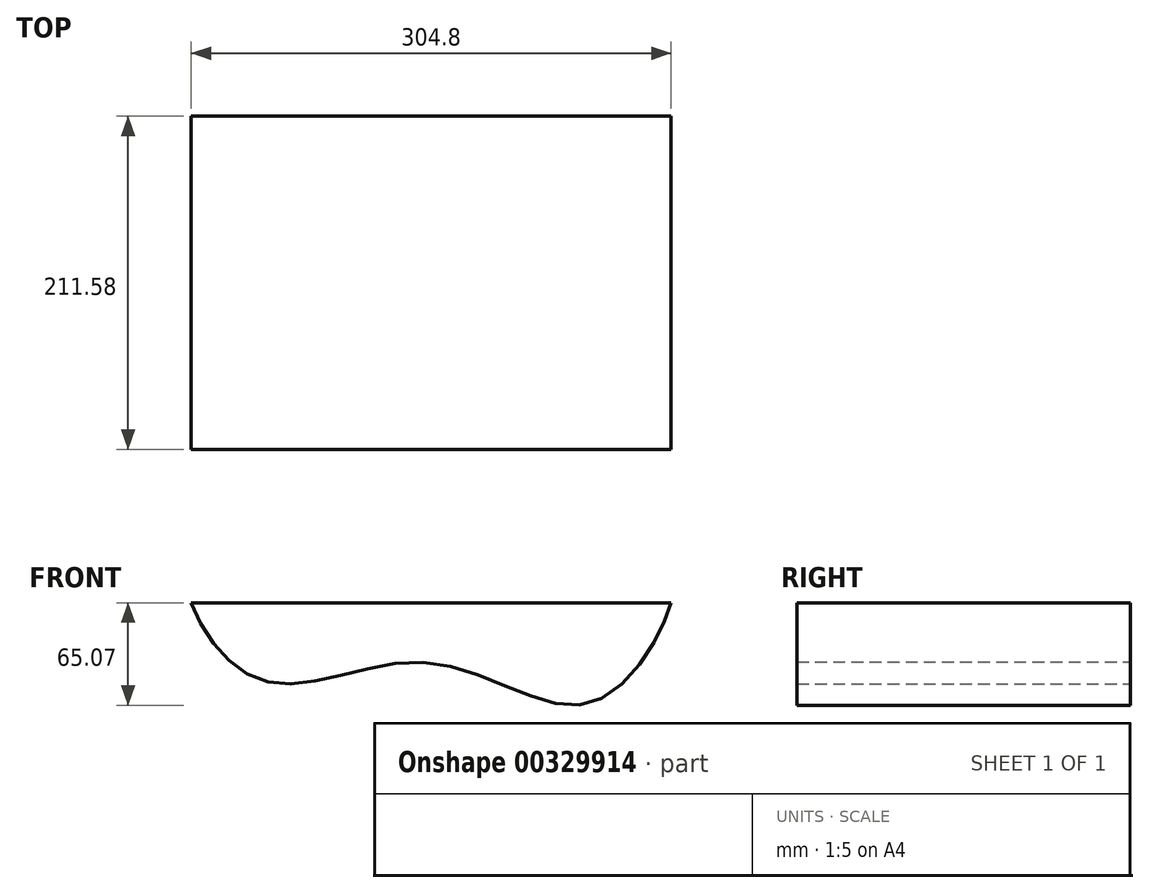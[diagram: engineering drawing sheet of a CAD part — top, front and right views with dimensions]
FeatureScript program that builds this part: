
annotation { "Feature Type Name" : "Feature", "Feature Type Description" : "" }
export const myFeature = defineFeature(function(context is Context, id is Id, definition is map)
    precondition{}
    {
        {
            var Q0;
            Q0=qCreatedBy(makeId("Front.planeOp"),FACE);
            var sketch = newSketch(context, id + "F0", { "sketchPlane" : qUnion([Q0])});
            skFitSpline(sketch, "E0", {"points": [v(-74.38, 17.7) * mm, v(-23.58, -33.1) * mm, v(78.02, -20.4) * mm, v(179.62, -45.8) * mm, v(230.42, 17.7) * mm], "startDerivative": vector(113.55, -303.34) * mm, "endDerivative": vector(59.58, 225.06) * mm});
            skLineSegment(sketch, "E1", {"start": v(-74.38, 17.7) * mm, "end": v(230.42, 17.7) * mm});
            skSolve(sketch);
        }
        {
            var Q0;
            Q0=makeQuery(id+"F0.imprint","IMPRINT",FACE,{"disambiguationData":[TD([[makeQuery(id+"F0.imprint","IMPRINT",EDGE,{"derivedFrom":sQuery(id+"F0.wireOp",EDGE,"E0")}),1.0]])]});
            extrude(context, id + "F1", {"entities" : qUnion([Q0]), "oppositeDirection" : true, "depth" : 211.58 * mm});
        }
    });
